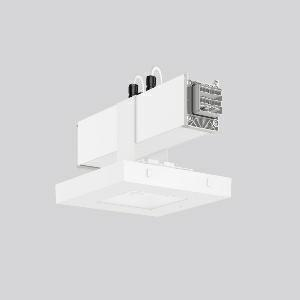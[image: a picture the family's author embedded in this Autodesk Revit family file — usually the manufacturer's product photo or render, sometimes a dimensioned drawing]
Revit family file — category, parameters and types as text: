
# Revit family: linedo_module_rf_9503rf_762_400_000_ba90
name_source: partatom
category: Lighting Fixtures
units: mm (PartAtom-declared; Revit-internal decimal feet)

## family parameters
Cut with Voids When Loaded = No
Host = Face
Light Source = No
Part Type = Normal
Room Calculation Point = No
Round Connector Dimension = Use Diameter
Shared = No

## types (1)
- LINEDO Module RF (1 x LED Modul 765, 420 lm, 6500)
    Apparent Load = 6 VA
    CIE Flux Codes = 48 88 100 100 100
    Color Rendering = 70
    Color Temperature = 6500
    Default Elevation = 1800 mm
    Description = LINEDO, 5,7 W, 420 lm, 765, white, on/off
Continuous line luminaire, L 330 B 198 H 170, CBS, emergency-420 lm, Stromkreis
    Height = 170 mm  [stored 0.557743 ft]
    Lamp = 1 x LED Modul 765
    Lamp Light Flux = 420 lm
    Lamp count = 1
    Length = 330 mm
    Lifetime = 50000 h
    Luminous efficacy = 74 lm/W
    Manufacturer = RZB
    ModVariant = No
    Model = 9503RF.762.400.000
    Mounting Place = Ceiling
    Mounting Type = Surface mounted, Pendant
    Number of Poles = 1
    OnlyDefault = Yes
    Power Factor = 1
    Product Name = LINEDO Module RF
    Product group = Continuous line luminaire system Linedo IP 54
    ProductGroupID = 314
    Protection Class = Protection class I
    Protection Degree = IP 54
    RLX_Detail_Level = 1
    RLX_Emergency_Light_Flux = 420 lm
    RLX_Emergency_Type = 3
    RLX_Emergency_Type_DB = Yes
    RlxData = <blob elided: 19985 chars, md5=dc350ff4>
    Socket = socket
    Standby Power = 0 W
    System Light Flux = 420 lm
    System Power = 6 W
    Type Comments = Product without accessories
    Type Image = 9503rw.762.434.000.jpg
    URL = http://relux.com
    VarID = ---
    Voltage = 230 V
    Voltage Range = 220-240 V
    Weight = 0.00 kg
    Width = 198 mm

note: [stored X ft] marks values corroborated as IEEE doubles in the binary element streams (Revit-internal decimal feet)

## geometry (parser evidence)
native form markers: Blend x4, Sweep x12
no freeform markers — native parametric forms only
